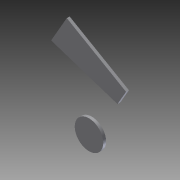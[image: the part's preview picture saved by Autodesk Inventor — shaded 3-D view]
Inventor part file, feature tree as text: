
AUTODESK INVENTOR PART (.ipt)
format: ipt  version: 2012 (Build 160160000, 160)  size: 78,336 bytes
history: native  units: in
note: dims shown in document units (in); Inventor stores cm internally (conversion verified against a paired STEP export)
features: extrude x1, sketch x1
ambient origin geometry x8: Origin, YZ Plane, XZ Plane, XY Plane, X Axis, Y Axis, Z Axis, Center Point
bodies: Solid1 (feature_tree)
feature tree (2):
  extrude  "Extrusion1"  Depth=1.25in
  sketch  "Sketch1"  dims[d3=0.125in d4=0.0in d5=1.25in d6=2.5in d7=3.0in d8=0.75in d9=1.375in d10=2.75in d11=1.25in]
